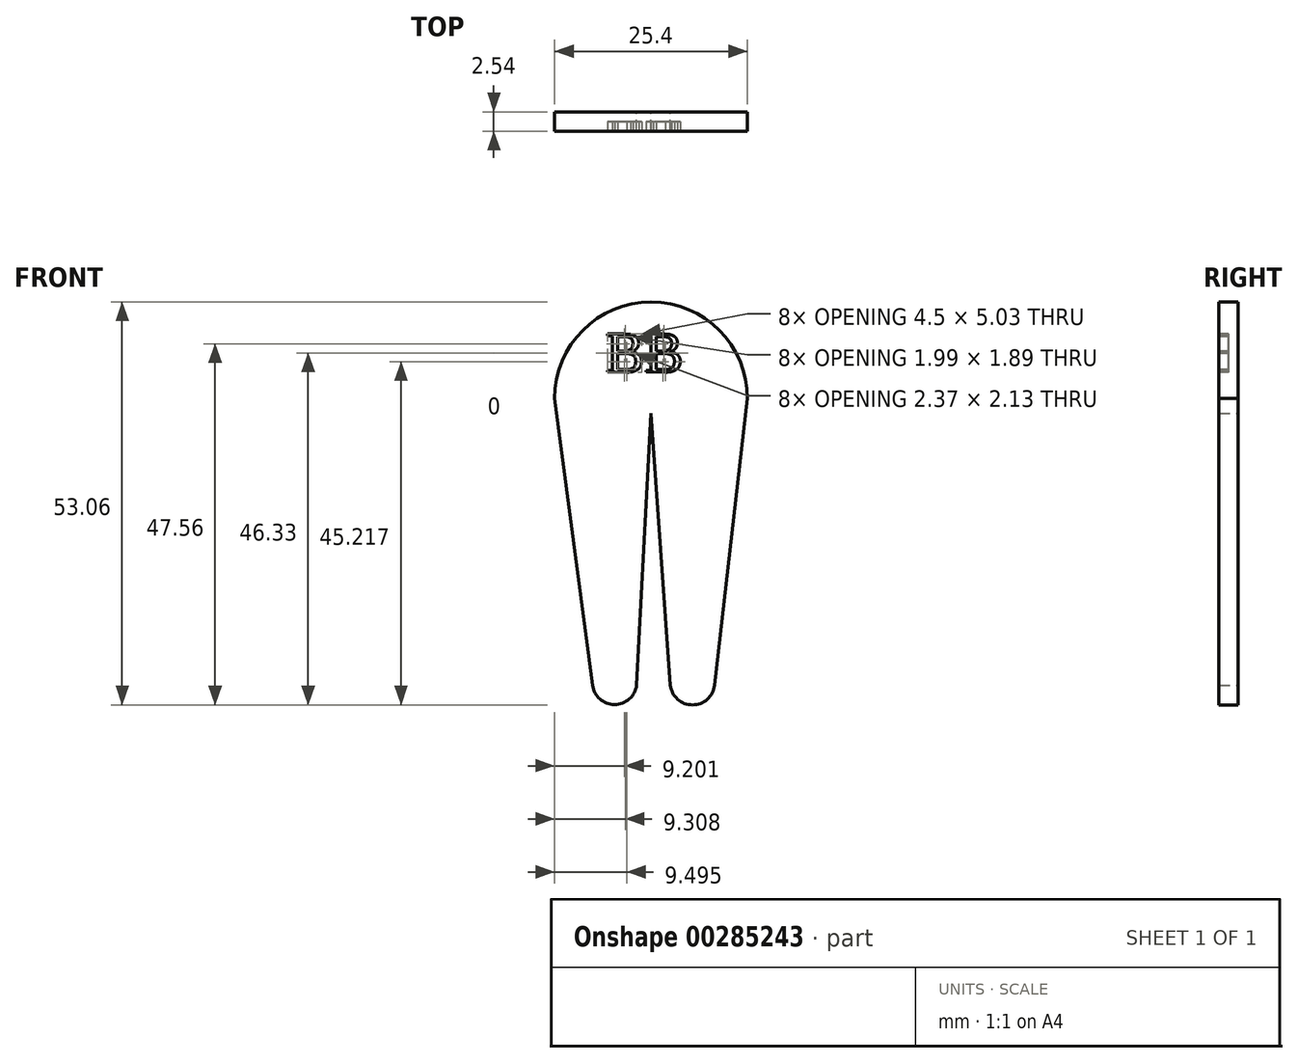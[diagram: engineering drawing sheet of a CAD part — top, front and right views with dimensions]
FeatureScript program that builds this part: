
annotation { "Feature Type Name" : "Feature", "Feature Type Description" : "" }
export const myFeature = defineFeature(function(context is Context, id is Id, definition is map)
    precondition{}
    {
        {
            var Q0;
            Q0=qCreatedBy(makeId("Front.planeOp"),FACE);
            var sketch = newSketch(context, id + "F0", { "sketchPlane" : qUnion([Q0])});
            skArc(sketch, "E0", {"start": v(12.73, 0) * mm, "mid": v(0.03, 12.7) * mm, "end": v(-12.67, 0) * mm});
            skLineSegment(sketch, "E1", {"start": v(-12.67, 0) * mm, "end": v(-7.68, -37.77) * mm});
            skLineSegment(sketch, "E2", {"start": v(12.73, 0) * mm, "end": v(8.39, -37.77) * mm});
            skArc(sketch, "E3", {"start": v(-7.68, -37.77) * mm, "mid": v(-4.78, -40.31) * mm, "end": v(-1.88, -37.77) * mm});
            skArc(sketch, "E4", {"start": v(2.57, -37.77) * mm, "mid": v(5.48, -40.36) * mm, "end": v(8.39, -37.77) * mm});
            skLineSegment(sketch, "E5", {"start": v(-1.88, -37.77) * mm, "end": v(0, -2) * mm});
            skLineSegment(sketch, "E6", {"start": v(0, -2) * mm, "end": v(2.57, -37.77) * mm});
            skSolve(sketch);
        }
        {
            var Q0;
            Q0 = qSketchRegion(id + "F0", true);
            extrude(context, id + "F1", {"entities" : qUnion([Q0]), "depth" : 2.54 * mm, "offsetDistance" : 25.4 * mm});
        }
        {
            var Q0;
            Q0=makeQuery(id+"F1.opExtrude","CAP_FACE",FACE,{"disambiguationData":[OSD([sQuery(id+"F0.wireOp",EDGE,"E0"),sQuery(id+"F0.wireOp",EDGE,"E1"),sQuery(id+"F0.wireOp",EDGE,"E2"),sQuery(id+"F0.wireOp",EDGE,"E3"),sQuery(id+"F0.wireOp",EDGE,"E4"),sQuery(id+"F0.wireOp",EDGE,"E5"),sQuery(id+"F0.wireOp",EDGE,"E6")])],"isStart":false});
            var sketch = newSketch(context, id + "F2", { "sketchPlane" : qUnion([Q0])});
            skText(sketch, "E7", { "text": "BB", "fontName": "Tinos-Regular.ttf"});
            const initialGuessF2  = {"E7": [-0.00594, 0.00348, 1, 0, 0.0055]};
            skSetInitialGuess(sketch, initialGuessF2);
            skSolve(sketch);
        }
        {
            var Q0;
            Q0 = qSketchRegion(id + "F2", true);
            extrude(context, id + "F3", {"entities" : qUnion([Q0]), "operationType" : NewBodyOperationType.REMOVE, "oppositeDirection" : true, "depth" : 1.27 * mm, "offsetDistance" : 25.4 * mm});
        }
    });
